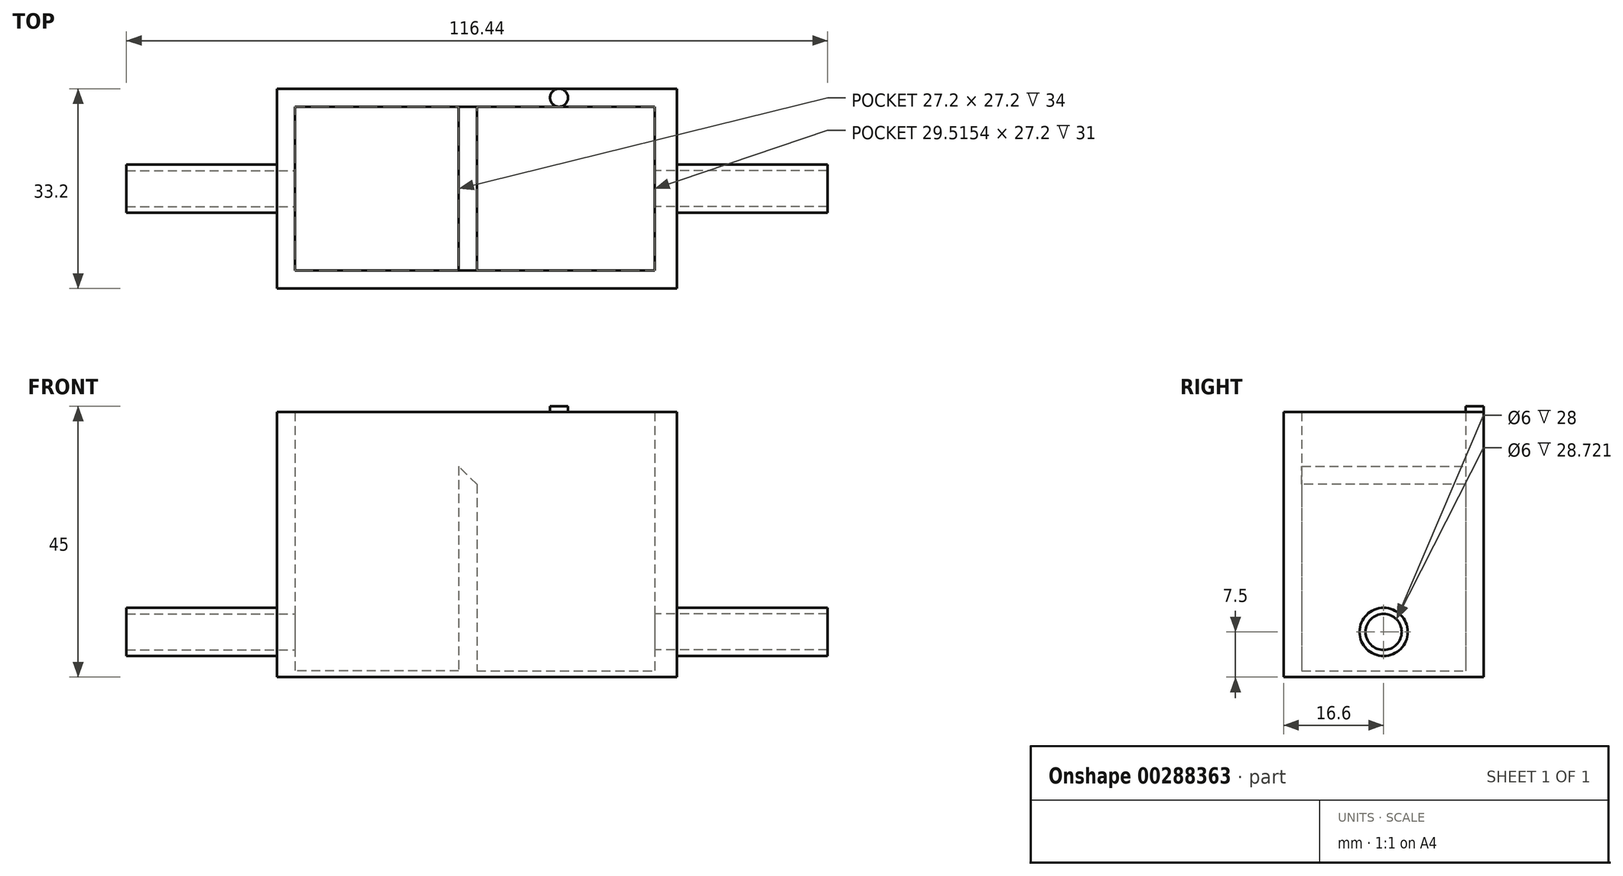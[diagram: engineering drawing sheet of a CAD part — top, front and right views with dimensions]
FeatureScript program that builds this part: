
annotation { "Feature Type Name" : "Feature", "Feature Type Description" : "" }
export const myFeature = defineFeature(function(context is Context, id is Id, definition is map)
    precondition{}
    {
        {
            var Q0;
            Q0=qCreatedBy(makeId("Top.planeOp"),FACE);
            var sketch = newSketch(context, id + "F0", { "sketchPlane" : qUnion([Q0])});
            skLineSegment(sketch, "E0.bottom", {"start": v(13.6, -13.6) * mm, "end": v(-13.6, -13.6) * mm});
            skLineSegment(sketch, "E0.top", {"start": v(13.6, 13.6) * mm, "end": v(-13.6, 13.6) * mm});
            skLineSegment(sketch, "E0.left", {"start": v(13.6, -13.6) * mm, "end": v(13.6, 13.6) * mm});
            skLineSegment(sketch, "E0.right", {"start": v(-13.6, -13.6) * mm, "end": v(-13.6, 13.6) * mm});
            skPoint(sketch, "E0.middle", {"position": v(0, 0) * mm});
            skLineSegment(sketch, "E1.0", {"start": v(16.6, 16.6) * mm, "end": v(-16.6, 16.6) * mm});
            skLineSegment(sketch, "E1.2", {"start": v(16.6, -16.6) * mm, "end": v(-16.6, -16.6) * mm});
            skLineSegment(sketch, "E1.3", {"start": v(-16.6, -16.6) * mm, "end": v(-16.6, 16.6) * mm});
            skLineSegment(sketch, "E2.bottom", {"start": v(-16.6, -3) * mm, "end": v(-36.6, -3) * mm});
            skLineSegment(sketch, "E2.top", {"start": v(-16.6, 3) * mm, "end": v(-36.6, 3) * mm});
            skLineSegment(sketch, "E2.left", {"start": v(-16.6, -3) * mm, "end": v(-16.6, 3) * mm});
            skPoint(sketch, "E2.middle", {"position": v(-26.6, 0) * mm});
            skLineSegment(sketch, "E3.left", {"start": v(16.6, -3) * mm, "end": v(16.6, 3) * mm});
            skPoint(sketch, "E3.middle.positionSnap0", {"position": v(16.6, 0) * mm});
            skPoint(sketch, "E3.centerSnap0", {"position": v(16.6, 0) * mm});
            skLineSegment(sketch, "E4.bottom", {"start": v(16.6, -16.6) * mm, "end": v(49.84, -16.6) * mm});
            skLineSegment(sketch, "E4.top", {"start": v(16.6, 16.6) * mm, "end": v(49.84, 16.6) * mm});
            skLineSegment(sketch, "E4.right", {"start": v(49.84, -16.6) * mm, "end": v(49.84, 16.6) * mm});
            skLineSegment(sketch, "E5", {"start": v(13.6, -13.6) * mm, "end": v(16.6, -13.6) * mm});
            skLineSegment(sketch, "E6", {"start": v(13.6, 13.6) * mm, "end": v(16.6, 13.6) * mm});
            skLineSegment(sketch, "E7.bottom", {"start": v(16.6, -13.6) * mm, "end": v(46.12, -13.6) * mm});
            skLineSegment(sketch, "E7.top", {"start": v(16.6, 13.6) * mm, "end": v(46.12, 13.6) * mm});
            skLineSegment(sketch, "E7.left", {"start": v(16.6, -13.6) * mm, "end": v(16.6, 13.6) * mm});
            skLineSegment(sketch, "E7.right", {"start": v(46.12, -13.6) * mm, "end": v(46.12, 13.6) * mm});
            skLineSegment(sketch, "E8", {"start": v(49.84, 3) * mm, "end": v(64.84, 3) * mm});
            skLineSegment(sketch, "E9", {"start": v(64.84, -3) * mm, "end": v(64.84, 3) * mm});
            skLineSegment(sketch, "E10", {"start": v(-36.6, -3) * mm, "end": v(-36.6, -2) * mm});
            skLineSegment(sketch, "E11", {"start": v(64.84, 0) * mm, "end": v(-36.6, 0) * mm, "construction": true});
            skLineSegment(sketch, "E12.MirrorCS", {"start": v(-36.6, 3) * mm, "end": v(-36.6, 2) * mm});
            skLineSegment(sketch, "E13", {"start": v(-36.6, -2) * mm, "end": v(-36.6, 2) * mm});
            skLineSegment(sketch, "E14", {"start": v(-36.6, -2) * mm, "end": v(-16.6, -2) * mm});
            skLineSegment(sketch, "E15", {"start": v(-36.6, 2) * mm, "end": v(-16.6, 2) * mm});
            skLineSegment(sketch, "E16", {"start": v(49.84, -2) * mm, "end": v(64.84, -2) * mm});
            skLineSegment(sketch, "E17.MirrorCS", {"start": v(49.84, 2) * mm, "end": v(64.84, 2) * mm});
            skLineSegment(sketch, "E18", {"start": v(64.84, -3) * mm, "end": v(49.84, -3) * mm});
            skCircle(sketch, "E19", {"center": v(0, 15.1) * mm, "radius": 1.5 * mm, "construction": true});
            skPoint(sketch, "E19.centerSnap0", {"position": v(0, 13.6) * mm});
            skSolve(sketch);
        }
        {
            var Q0;
            Q0=makeQuery(id+"F0.imprint","IMPRINT",FACE,{"disambiguationData":[TD([[makeQuery(id+"F0.imprint","IMPRINT",EDGE,{"derivedFrom":sQuery(id+"F0.wireOp",EDGE,"E0.bottom")}),1.0]])]});
            extrude(context, id + "F1", {"entities" : qUnion([Q0]), "depth" : 44 * mm});
        }
        {
            var Q0;
            Q0=makeQuery(id+"F0.imprint","IMPRINT",FACE,{"disambiguationData":[TD([[makeQuery(id+"F0.imprint","IMPRINT",EDGE,{"derivedFrom":sQuery(id+"F0.wireOp",EDGE,"E0.bottom")}),-1.0]])]});
            var Q1;
            {var subQ3=sQuery(id+"F0.wireOp",EDGE,"E7.bottom");Q1=makeQuery(id+"F0.imprint","IMPRINT",FACE,{"disambiguationData":[TD([[makeQuery(id+"F0.imprint","IMPRINT",EDGE,{"derivedFrom":subQ3}),1.0]])]});}
            extrude(context, id + "F2", {"entities" : qUnion([Q0, Q1]), "operationType" : NewBodyOperationType.ADD, "depth" : 1 * mm});
        }
        {
            var Q0;
            Q0=makeQuery(id+"F0.imprint","IMPRINT",FACE,{"disambiguationData":[TD([[makeQuery(id+"F0.imprint","IMPRINT",EDGE,{"derivedFrom":sQuery(id+"F0.wireOp",EDGE,"E0.left")}),-1.0]])]});
            extrude(context, id + "F3", {"entities" : qUnion([Q0]), "operationType" : NewBodyOperationType.ADD, "depth" : 37 * mm});
        }
        {
            var Q0;
            Q0=makeQuery(id+"F1.opExtrude","SWEPT_FACE",FACE,{"disambiguationData":[OSD([sQuery(id+"F0.wireOp",EDGE,"E1.3"),sQuery(id+"F0.wireOp",EDGE,"E2.left")])]});
            var sketch = newSketch(context, id + "F4", { "sketchPlane" : qUnion([Q0])});
            skCircle(sketch, "E20", {"center": v(0, 7.5) * mm, "radius": 3 * mm});
            skCircle(sketch, "E21.0", {"center": v(0, 7.5) * mm, "radius": 4 * mm});
            skSolve(sketch);
        }
        {
            var Q0;
            Q0 = qSketchRegion(id + "F4", true);
            extrude(context, id + "F5", {"entities" : qUnion([Q0]), "operationType" : NewBodyOperationType.ADD, "depth" : 25 * mm});
        }
        {
            var Q0;
            Q0=makeQuery(id+"F5.boolean.opBoolean","SPLIT",FACE,{"disambiguationData":[TD([makeQuery(id+"F5.opExtrude","SWEPT_FACE",FACE,{"disambiguationData":[OSD([sQuery(id+"F4.wireOp",EDGE,"E20")])]})])],"derivedFrom":makeQuery(id+"F1.opExtrude","SWEPT_FACE",FACE,{"disambiguationData":[OSD([sQuery(id+"F0.wireOp",EDGE,"E1.3"),sQuery(id+"F0.wireOp",EDGE,"E2.left")])]})});
            extrude(context, id + "F6", {"entities" : qUnion([Q0]), "operationType" : NewBodyOperationType.REMOVE, "oppositeDirection" : true, "depth" : 5 * mm});
        }
        {
            var Q0;
            Q0=makeQuery(id+"F1.opExtrude","SWEPT_FACE",FACE,{"disambiguationData":[OSD([sQuery(id+"F0.wireOp",EDGE,"E4.right")])]});
            var sketch = newSketch(context, id + "F7", { "sketchPlane" : qUnion([Q0])});
            skCircle(sketch, "E22", {"center": v(0, 7.5) * mm, "radius": 3 * mm});
            skCircle(sketch, "E23.0", {"center": v(0, 7.5) * mm, "radius": 4 * mm});
            skSolve(sketch);
        }
        {
            var Q0;
            Q0=makeQuery(id+"F7.imprint","IMPRINT",FACE,{"disambiguationData":[TD([[makeQuery(id+"F7.imprint","IMPRINT",EDGE,{"derivedFrom":sQuery(id+"F7.wireOp",EDGE,"E22")}),-1.0]])]});
            extrude(context, id + "F8", {"entities" : qUnion([Q0]), "operationType" : NewBodyOperationType.ADD, "depth" : 25 * mm});
        }
        {
            var Q0;
            Q0=makeQuery(id+"F8.boolean.opBoolean","SPLIT",FACE,{"disambiguationData":[TD([makeQuery(id+"F8.opExtrude","SWEPT_FACE",FACE,{"disambiguationData":[OSD([sQuery(id+"F7.wireOp",EDGE,"E22")])]})])],"derivedFrom":makeQuery(id+"F1.opExtrude","SWEPT_FACE",FACE,{"disambiguationData":[OSD([sQuery(id+"F0.wireOp",EDGE,"E4.right")])]})});
            extrude(context, id + "F9", {"entities" : qUnion([Q0]), "operationType" : NewBodyOperationType.REMOVE, "oppositeDirection" : true, "depth" : 5 * mm});
        }
        {
            var Q0;
            Q0=makeQuery(id+"F3.opExtrude","CAP_EDGE",EDGE,{"disambiguationData":[OSD([sQuery(id+"F0.wireOp",EDGE,"E7.left")])],"isStart":false});
            chamfer(context, id + "F10", {"entities" : qUnion([Q0]), "width" : 5 * mm, "tangentPropagation" : true});
        }
        {
            var Q0;
            Q0=makeQuery(id+"F1.opExtrude","CAP_FACE",FACE,{"disambiguationData":[OSD([sQuery(id+"F0.wireOp",EDGE,"E0.bottom"),sQuery(id+"F0.wireOp",EDGE,"E0.top"),sQuery(id+"F0.wireOp",EDGE,"E0.right"),sQuery(id+"F0.wireOp",EDGE,"E1.0"),sQuery(id+"F0.wireOp",EDGE,"E1.2"),sQuery(id+"F0.wireOp",EDGE,"E1.3"),sQuery(id+"F0.wireOp",EDGE,"E2.left"),sQuery(id+"F0.wireOp",EDGE,"E4.bottom"),sQuery(id+"F0.wireOp",EDGE,"E4.top"),sQuery(id+"F0.wireOp",EDGE,"E4.right"),sQuery(id+"F0.wireOp",EDGE,"E5"),sQuery(id+"F0.wireOp",EDGE,"E6"),sQuery(id+"F0.wireOp",EDGE,"E7.bottom"),sQuery(id+"F0.wireOp",EDGE,"E7.top"),sQuery(id+"F0.wireOp",EDGE,"E7.right")])],"isStart":false});
            var sketch = newSketch(context, id + "F11", { "sketchPlane" : qUnion([Q0])});
            skCircle(sketch, "E24", {"center": v(30.25, 15.1) * mm, "radius": 1.5 * mm});
            skSolve(sketch);
        }
        {
            var Q0;
            {var subQ0=sQuery(id+"F11.wireOp",EDGE,"E24");var subQ1=makeQuery(id+"F11.imprint","INTERSECT",VERTEX,{"derivedFrom":[makeQuery(id+"F1.opExtrude","CAP_EDGE",EDGE,{"disambiguationData":[OSD([sQuery(id+"F0.wireOp",EDGE,"E1.0"),sQuery(id+"F0.wireOp",EDGE,"E4.top")])],"isStart":false}),subQ0]});Q0=makeQuery(id+"F11.imprint","IMPRINT",FACE,{"disambiguationData":[TD([[makeQuery(id+"F11.imprint","IMPRINT",EDGE,{"disambiguationData":[TD([[subQ1,-1.0]])],"derivedFrom":subQ0}),1.0]])]});}
            extrude(context, id + "F12", {"entities" : qUnion([Q0]), "operationType" : NewBodyOperationType.ADD, "depth" : 1 * mm});
        }
    });
